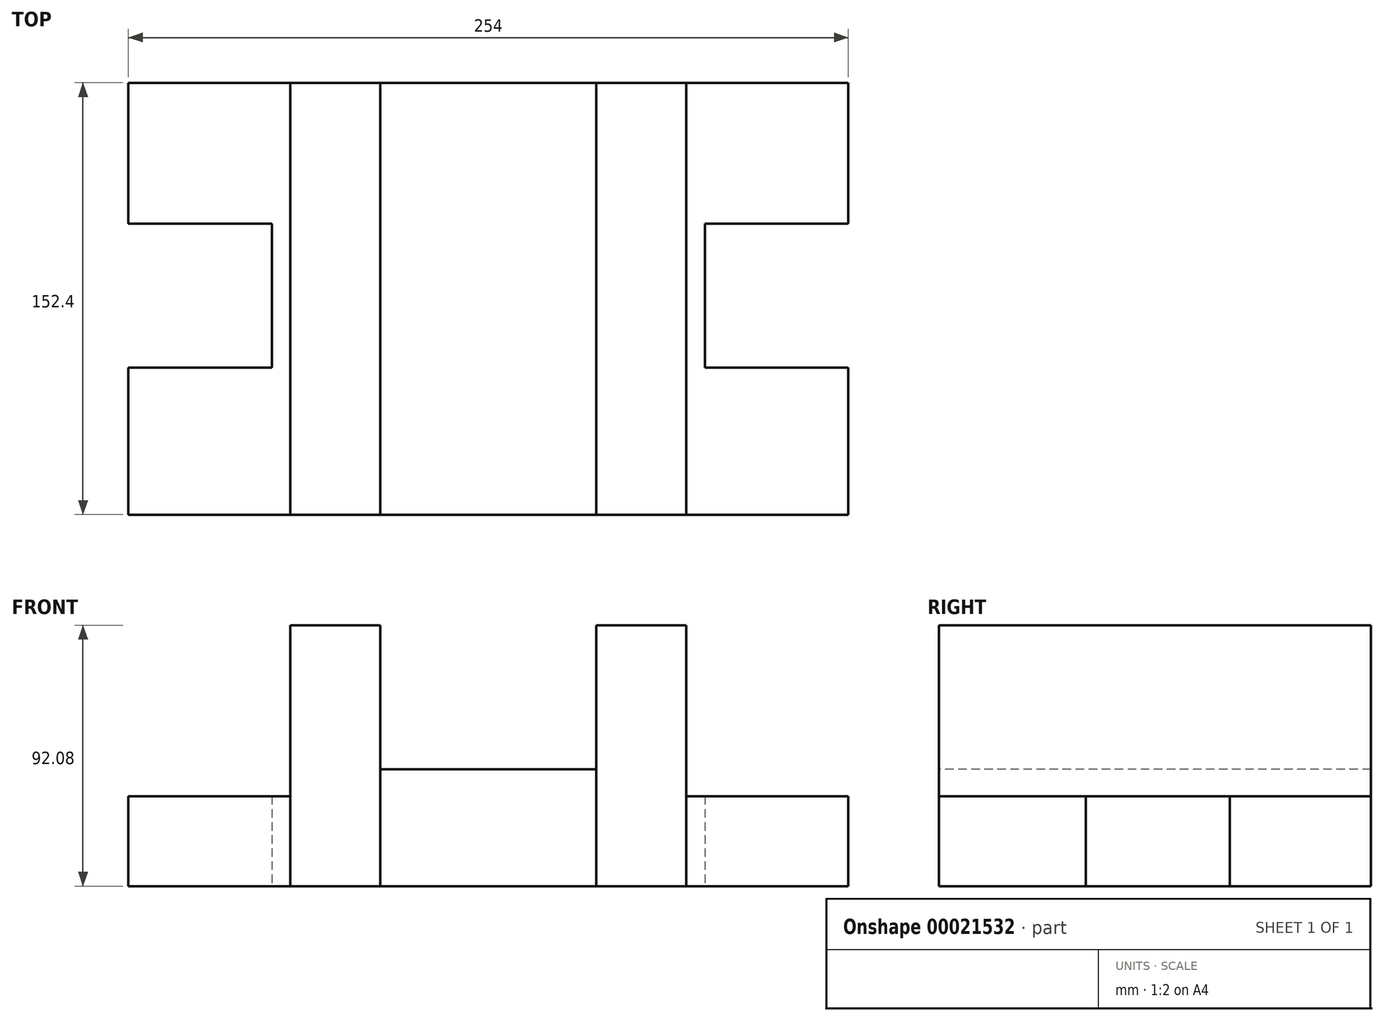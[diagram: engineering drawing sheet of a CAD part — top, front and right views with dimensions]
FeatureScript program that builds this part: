
annotation { "Feature Type Name" : "Feature", "Feature Type Description" : "" }
export const myFeature = defineFeature(function(context is Context, id is Id, definition is map)
    precondition{}
    {
        {
            var Q0;
            Q0=qCreatedBy(makeId("Top.planeOp"),FACE);
            var sketch = newSketch(context, id + "F0", { "sketchPlane" : qUnion([Q0])});
            skLineSegment(sketch, "E0.bottom", {"start": v(69.85, 100.56) * mm, "end": v(127, 100.56) * mm});
            skLineSegment(sketch, "E0.top", {"start": v(0, -51.84) * mm, "end": v(127, -51.84) * mm});
            skLineSegment(sketch, "E0.right", {"start": v(127, 100.56) * mm, "end": v(127, -51.84) * mm});
            skLineSegment(sketch, "E1", {"start": v(127, 50.8) * mm, "end": v(76.38, 50.8) * mm});
            skLineSegment(sketch, "E2", {"start": v(76.38, 50.8) * mm, "end": v(76.38, 0) * mm});
            skLineSegment(sketch, "E3", {"start": v(76.38, 0) * mm, "end": v(127, 0) * mm});
            skLineSegment(sketch, "E4", {"start": v(38.1, 100.56) * mm, "end": v(38.1, -51.84) * mm});
            skLineSegment(sketch, "E5", {"start": v(69.85, 100.56) * mm, "end": v(69.85, -51.84) * mm});
            skLineSegment(sketch, "E6", {"start": v(0, 100.56) * mm, "end": v(38.1, 100.56) * mm});
            skLineSegment(sketch, "E7", {"start": v(38.1, 100.56) * mm, "end": v(69.85, 100.56) * mm});
            skLineSegment(sketch, "E8.MirrorCS", {"start": v(0, 100.56) * mm, "end": v(-38.1, 100.56) * mm});
            skLineSegment(sketch, "E9.MirrorCS", {"start": v(-38.1, 100.56) * mm, "end": v(-38.1, -51.84) * mm});
            skLineSegment(sketch, "E10.MirrorCS", {"start": v(-69.85, 100.56) * mm, "end": v(-69.85, -51.84) * mm});
            skLineSegment(sketch, "E11.MirrorCS", {"start": v(0, -51.84) * mm, "end": v(-127, -51.84) * mm});
            skLineSegment(sketch, "E12.MirrorCS", {"start": v(-127, 100.56) * mm, "end": v(-127, -51.84) * mm});
            skLineSegment(sketch, "E13.MirrorCS", {"start": v(-76.38, 0) * mm, "end": v(-127, 0) * mm});
            skLineSegment(sketch, "E14.MirrorCS", {"start": v(-76.38, 50.8) * mm, "end": v(-76.38, 0) * mm});
            skLineSegment(sketch, "E15.MirrorCS", {"start": v(-127, 50.8) * mm, "end": v(-76.38, 50.8) * mm});
            skLineSegment(sketch, "E16.MirrorCS", {"start": v(-69.85, 100.56) * mm, "end": v(-127, 100.56) * mm});
            skLineSegment(sketch, "E17.MirrorCS", {"start": v(-38.1, 100.56) * mm, "end": v(-69.85, 100.56) * mm});
            skLineSegment(sketch, "E18", {"start": v(0, -51.84) * mm, "end": v(0, 24.36) * mm});
            skSolve(sketch);
        }
        {
            var Q0;
            {var subQ2=sQuery(id+"F0.wireOp",EDGE,"E9.MirrorCS");Q0=makeQuery(id+"F0.imprint","IMPRINT",FACE,{"disambiguationData":[TD([[makeQuery(id+"F0.imprint","IMPRINT",EDGE,{"derivedFrom":subQ2}),-1.0]])]});}
            var Q1;
            {var subQ1=sQuery(id+"F0.wireOp",EDGE,"E4");Q1=makeQuery(id+"F0.imprint","IMPRINT",FACE,{"disambiguationData":[TD([[makeQuery(id+"F0.imprint","IMPRINT",EDGE,{"derivedFrom":subQ1}),1.0]])]});}
            extrude(context, id + "F1", {"entities" : qUnion([Q0, Q1]), "depth" : 92.07 * mm});
        }
        {
            var Q0;
            {var subQ3=sQuery(id+"F0.wireOp",EDGE,"E13.MirrorCS");Q0=makeQuery(id+"F0.imprint","IMPRINT",FACE,{"disambiguationData":[TD([[makeQuery(id+"F0.imprint","IMPRINT",EDGE,{"derivedFrom":subQ3}),1.0]])]});}
            var Q1;
            {var subQ6=sQuery(id+"F0.wireOp",EDGE,"E0.bottom");Q1=makeQuery(id+"F0.imprint","IMPRINT",FACE,{"disambiguationData":[TD([[makeQuery(id+"F0.imprint","IMPRINT",EDGE,{"derivedFrom":subQ6}),-1.0]])]});}
            extrude(context, id + "F2", {"entities" : qUnion([Q0, Q1]), "depth" : 31.75 * mm});
        }
        {
            var Q0;
            {var subQ4=sQuery(id+"F0.wireOp",EDGE,"E4");Q0=makeQuery(id+"F0.imprint","IMPRINT",FACE,{"disambiguationData":[TD([[makeQuery(id+"F0.imprint","IMPRINT",EDGE,{"derivedFrom":subQ4}),-1.0]])]});}
            extrude(context, id + "F3", {"entities" : qUnion([Q0]), "depth" : 41.27 * mm});
        }
    });
